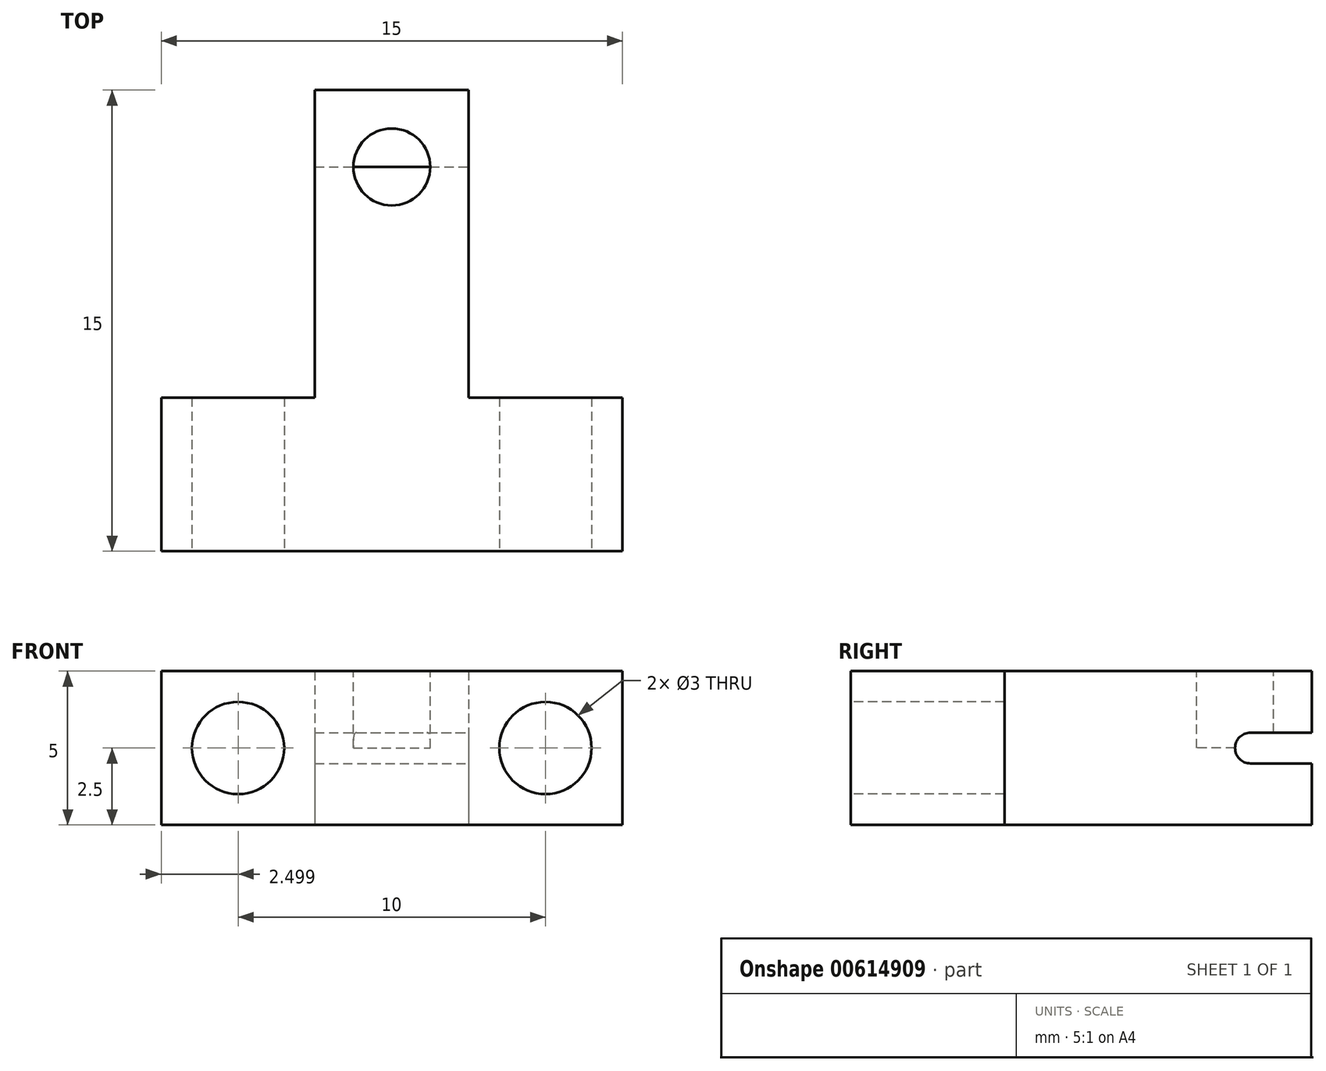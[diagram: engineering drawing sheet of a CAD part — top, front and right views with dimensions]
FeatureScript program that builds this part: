
annotation { "Feature Type Name" : "Feature", "Feature Type Description" : "" }
export const myFeature = defineFeature(function(context is Context, id is Id, definition is map)
    precondition{}
    {
        {
            var Q0;
            Q0=qCreatedBy(makeId("Front.planeOp"),FACE);
            var sketch = newSketch(context, id + "F0", { "sketchPlane" : qUnion([Q0])});
            skLineSegment(sketch, "E0.bottom", {"start": v(-1.35, 4.7) * mm, "end": v(3.65, 4.7) * mm});
            skLineSegment(sketch, "E0.top", {"start": v(-1.35, -0.3) * mm, "end": v(3.65, -0.3) * mm});
            skLineSegment(sketch, "E0.left", {"start": v(-1.35, 4.7) * mm, "end": v(-1.35, -0.3) * mm});
            skLineSegment(sketch, "E0.right", {"start": v(3.65, 4.7) * mm, "end": v(3.65, -0.3) * mm});
            skSolve(sketch);
        }
        {
            var Q0;
            Q0 = qSketchRegion(id + "F0", true);
            extrude(context, id + "F1", {"entities" : qUnion([Q0]), "depth" : 15 * mm, "offsetDistance" : 25.4 * mm});
        }
        {
            var Q0;
            Q0=makeQuery(id+"F1.opExtrude","SWEPT_FACE",FACE,{"disambiguationData":[OSD([sQuery(id+"F0.wireOp",EDGE,"E0.right")])]});
            var sketch = newSketch(context, id + "F2", { "sketchPlane" : qUnion([Q0])});
            skLineSegment(sketch, "E1.bottom", {"start": v(-15, 4.7) * mm, "end": v(-10, 4.7) * mm});
            skLineSegment(sketch, "E1.top", {"start": v(-15, -0.3) * mm, "end": v(-10, -0.3) * mm});
            skLineSegment(sketch, "E1.left", {"start": v(-15, 4.7) * mm, "end": v(-15, -0.3) * mm});
            skLineSegment(sketch, "E1.right", {"start": v(-10, 4.7) * mm, "end": v(-10, -0.3) * mm});
            skSolve(sketch);
        }
        {
            var Q0;
            Q0=makeQuery(id+"F2.imprint","IMPRINT",FACE,{"disambiguationData":[TD([[makeQuery(id+"F2.imprint","IMPRINT",EDGE,{"derivedFrom":sQuery(id+"F2.wireOp",EDGE,"E1.bottom")}),-1.0]])]});
            extrude(context, id + "F3", {"entities" : qUnion([Q0]), "operationType" : NewBodyOperationType.ADD, "depth" : 5 * mm, "offsetDistance" : 25 * mm});
        }
        {
            var Q0;
            Q0=makeQuery(id+"F2.imprint","IMPRINT",FACE,{"disambiguationData":[TD([[makeQuery(id+"F2.imprint","IMPRINT",EDGE,{"derivedFrom":sQuery(id+"F2.wireOp",EDGE,"E1.bottom")}),-1.0]])]});
            extrude(context, id + "F4", {"entities" : qUnion([Q0]), "operationType" : NewBodyOperationType.ADD, "oppositeDirection" : true, "depth" : 10 * mm, "offsetDistance" : 25 * mm});
        }
        {
            var Q0;
            {var subQ0=sQuery(id+"F2.wireOp",EDGE,"E1.left");Q0=makeQuery(id+"F4.boolean.opBoolean","MERGE",FACE,{"derivedFrom":[makeQuery(id+"F3.boolean.opBoolean","MERGE",FACE,{"derivedFrom":[makeQuery(id+"F1.opExtrude","CAP_FACE",FACE,{"disambiguationData":[OSD([sQuery(id+"F0.wireOp",EDGE,"E0.bottom"),sQuery(id+"F0.wireOp",EDGE,"E0.top"),sQuery(id+"F0.wireOp",EDGE,"E0.left"),sQuery(id+"F0.wireOp",EDGE,"E0.right")])],"isStart":false}),makeQuery(id+"F3.opExtrude","SWEPT_FACE",FACE,{"disambiguationData":[OSD([subQ0])]})]}),makeQuery(id+"F4.opExtrude","SWEPT_FACE",FACE,{"disambiguationData":[OSD([subQ0])]})]});}
            var sketch = newSketch(context, id + "F5", { "sketchPlane" : qUnion([Q0])});
            skCircle(sketch, "E2", {"center": v(6.15, 2.2) * mm, "radius": 1.5 * mm});
            skPoint(sketch, "E2.centerSnap0", {"position": v(8.65, 2.2) * mm});
            skCircle(sketch, "E3", {"center": v(-3.85, 2.2) * mm, "radius": 1.5 * mm});
            skSolve(sketch);
        }
        {
            var Q0;
            Q0=makeQuery(id+"F5.imprint","IMPRINT",FACE,{"disambiguationData":[TD([[makeQuery(id+"F5.imprint","IMPRINT",EDGE,{"derivedFrom":sQuery(id+"F5.wireOp",EDGE,"E3")}),1.0]])]});
            var Q1;
            Q1=makeQuery(id+"F5.imprint","IMPRINT",FACE,{"disambiguationData":[TD([[makeQuery(id+"F5.imprint","IMPRINT",EDGE,{"derivedFrom":sQuery(id+"F5.wireOp",EDGE,"E2")}),1.0]])]});
            extrude(context, id + "F6", {"entities" : qUnion([Q0, Q1]), "operationType" : NewBodyOperationType.REMOVE, "oppositeDirection" : true, "depth" : 5 * mm, "offsetDistance" : 25 * mm});
        }
        {
            var Q0;
            Q0=makeQuery(id+"F1.opExtrude","SWEPT_FACE",FACE,{"disambiguationData":[OSD([sQuery(id+"F0.wireOp",EDGE,"E0.right")])]});
            var sketch = newSketch(context, id + "F7", { "sketchPlane" : qUnion([Q0])});
            skCircle(sketch, "E4", {"center": v(-2, 2.2) * mm, "radius": 0.5 * mm});
            skPoint(sketch, "E4.centerSnap0", {"position": v(0, 2.2) * mm});
            skLineSegment(sketch, "E5", {"start": v(-2, 1.7) * mm, "end": v(0, 1.7) * mm});
            skLineSegment(sketch, "E6", {"start": v(-2, 2.7) * mm, "end": v(0, 2.7) * mm});
            skSolve(sketch);
        }
        {
            var Q0;
            {var subQ0=sQuery(id+"F7.wireOp",EDGE,"E4");var subQ1=makeQuery(id+"F7.imprint","INTERSECT",VERTEX,{"derivedFrom":[subQ0,sQuery(id+"F7.wireOp",EDGE,"E5")]});Q0=makeQuery(id+"F7.imprint","IMPRINT",FACE,{"disambiguationData":[TD([[makeQuery(id+"F7.imprint","IMPRINT",EDGE,{"disambiguationData":[TD([[subQ1,1.0]])],"derivedFrom":subQ0}),1.0]])]});}
            var Q1;
            {var subQ0=sQuery(id+"F7.wireOp",EDGE,"E5");Q1=makeQuery(id+"F7.imprint","IMPRINT",FACE,{"disambiguationData":[TD([[makeQuery(id+"F7.imprint","IMPRINT",EDGE,{"derivedFrom":subQ0}),1.0]])]});}
            extrude(context, id + "F8", {"entities" : qUnion([Q0, Q1]), "operationType" : NewBodyOperationType.REMOVE, "oppositeDirection" : true, "depth" : 5 * mm, "offsetDistance" : 25 * mm});
        }
        {
            var Q0;
            {var subQ0=sQuery(id+"F2.wireOp",EDGE,"E1.bottom");Q0=makeQuery(id+"F4.boolean.opBoolean","MERGE",FACE,{"derivedFrom":[makeQuery(id+"F3.boolean.opBoolean","MERGE",FACE,{"derivedFrom":[makeQuery(id+"F1.opExtrude","SWEPT_FACE",FACE,{"disambiguationData":[OSD([sQuery(id+"F0.wireOp",EDGE,"E0.bottom")])]}),makeQuery(id+"F3.opExtrude","SWEPT_FACE",FACE,{"disambiguationData":[OSD([subQ0])]})]}),makeQuery(id+"F4.opExtrude","SWEPT_FACE",FACE,{"disambiguationData":[OSD([subQ0])]})]});}
            var sketch = newSketch(context, id + "F9", { "sketchPlane" : qUnion([Q0])});
            skCircle(sketch, "E7", {"center": v(1.15, -2.5) * mm, "radius": 1.25 * mm});
            skPoint(sketch, "E7.centerSnap0", {"position": v(1.15, 0) * mm});
            skSolve(sketch);
        }
        {
            var Q0;
            Q0=makeQuery(id+"F9.imprint","IMPRINT",FACE,{"disambiguationData":[TD([[makeQuery(id+"F9.imprint","IMPRINT",EDGE,{"derivedFrom":sQuery(id+"F9.wireOp",EDGE,"E7")}),1.0]])]});
            extrude(context, id + "F10", {"entities" : qUnion([Q0]), "operationType" : NewBodyOperationType.REMOVE, "oppositeDirection" : true, "depth" : 2.5 * mm, "offsetDistance" : 25 * mm});
        }
    });
